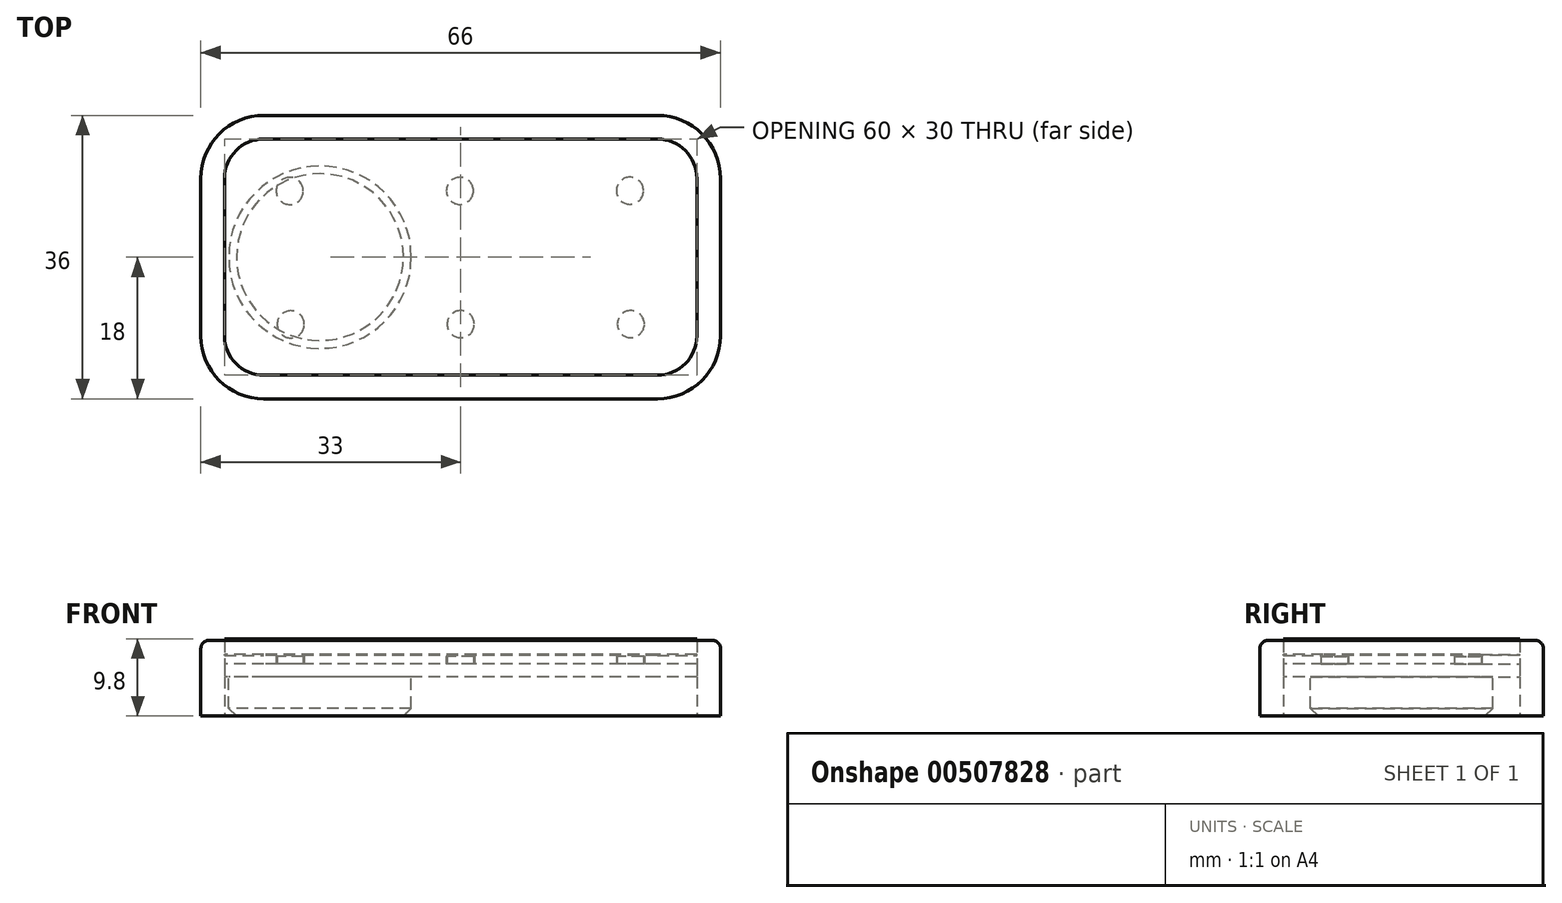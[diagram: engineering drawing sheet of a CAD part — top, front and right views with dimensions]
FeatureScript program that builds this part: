
annotation { "Feature Type Name" : "Feature", "Feature Type Description" : "" }
export const myFeature = defineFeature(function(context is Context, id is Id, definition is map)
    precondition{}
    {
        {
            var Q0;
            Q0=qCreatedBy(makeId("Top.planeOp"),FACE);
            var sketch = newSketch(context, id + "F0", { "sketchPlane" : qUnion([Q0])});
            skLineSegment(sketch, "E0.bottom", {"start": v(25, 15) * mm, "end": v(-25, 15) * mm});
            skLineSegment(sketch, "E0.top", {"start": v(25, -15) * mm, "end": v(-25, -15) * mm});
            skLineSegment(sketch, "E0.left", {"start": v(30, 10) * mm, "end": v(30, -10) * mm});
            skLineSegment(sketch, "E0.right", {"start": v(-30, 10) * mm, "end": v(-30, -10) * mm});
            skPoint(sketch, "E0.middle", {"position": v(0, 0) * mm});
            skPoint(sketch, "E1.visualSharp", {"position": v(-30, 15) * mm});
            skArc(sketch, "E1.filletArc", {"start": v(-25, 15) * mm, "mid": v(-28.54, 13.54) * mm, "end": v(-30, 10) * mm});
            skPoint(sketch, "E2.visualSharp", {"position": v(30, 15) * mm});
            skArc(sketch, "E2.filletArc", {"start": v(30, 10) * mm, "mid": v(28.54, 13.54) * mm, "end": v(25, 15) * mm});
            skPoint(sketch, "E3.visualSharp", {"position": v(30, -15) * mm});
            skArc(sketch, "E3.filletArc", {"start": v(25, -15) * mm, "mid": v(28.54, -13.54) * mm, "end": v(30, -10) * mm});
            skPoint(sketch, "E4.visualSharp", {"position": v(-30, -15) * mm});
            skArc(sketch, "E4.filletArc", {"start": v(-30, -10) * mm, "mid": v(-28.54, -13.54) * mm, "end": v(-25, -15) * mm});
            skArc(sketch, "E5.0", {"start": v(33, 10) * mm, "mid": v(30.66, 15.66) * mm, "end": v(25, 18) * mm});
            skLineSegment(sketch, "E5.1", {"start": v(33, 10) * mm, "end": v(33, -10) * mm});
            skLineSegment(sketch, "E5.2", {"start": v(25, 18) * mm, "end": v(-25, 18) * mm});
            skArc(sketch, "E5.3", {"start": v(25, -18) * mm, "mid": v(30.66, -15.66) * mm, "end": v(33, -10) * mm});
            skArc(sketch, "E5.4", {"start": v(-25, 18) * mm, "mid": v(-30.66, 15.66) * mm, "end": v(-33, 10) * mm});
            skLineSegment(sketch, "E5.5", {"start": v(-33, 10) * mm, "end": v(-33, -10) * mm});
            skArc(sketch, "E5.6", {"start": v(-33, -10) * mm, "mid": v(-30.66, -15.66) * mm, "end": v(-25, -18) * mm});
            skLineSegment(sketch, "E5.7", {"start": v(25, -18) * mm, "end": v(-25, -18) * mm});
            skSolve(sketch);
        }
        {
            var Q0;
            Q0=makeQuery(id+"F0.imprint","IMPRINT",FACE,{"disambiguationData":[TD([[makeQuery(id+"F0.imprint","IMPRINT",EDGE,{"derivedFrom":sQuery(id+"F0.wireOp",EDGE,"E0.bottom")}),1.0]])]});
            var Q1;
            Q1 = qConstructionFilter(qBodyType(qCreatedBy(id + "F0" ,EDGE), BodyType.WIRE), ConstructionObject.NO);
            extrude(context, id + "F1", {"entities" : qUnion([Q0]), "surfaceEntities" : qUnion([Q1]), "depth" : 1.6 * mm});
        }
        {
            var Q0;
            Q0=makeQuery(id+"F1.opExtrude","CAP_FACE",FACE,{"disambiguationData":[OSD([sQuery(id+"F0.wireOp",EDGE,"E0.bottom"),sQuery(id+"F0.wireOp",EDGE,"E0.top"),sQuery(id+"F0.wireOp",EDGE,"E0.left"),sQuery(id+"F0.wireOp",EDGE,"E0.right"),sQuery(id+"F0.wireOp",EDGE,"E1.filletArc"),sQuery(id+"F0.wireOp",EDGE,"E2.filletArc"),sQuery(id+"F0.wireOp",EDGE,"E3.filletArc"),sQuery(id+"F0.wireOp",EDGE,"E4.filletArc")])],"isStart":false});
            extrude(context, id + "F2", {"entities" : qUnion([Q0]), "depth" : 3.2 * mm});
        }
        {
            var Q0;
            Q0=makeQuery(id+"F2.opExtrude","CAP_FACE",FACE,{"disambiguationData":[OSD([sQuery(id+"F0.wireOp",EDGE,"E0.bottom"),sQuery(id+"F0.wireOp",EDGE,"E0.top"),sQuery(id+"F0.wireOp",EDGE,"E0.left"),sQuery(id+"F0.wireOp",EDGE,"E0.right"),sQuery(id+"F0.wireOp",EDGE,"E1.filletArc"),sQuery(id+"F0.wireOp",EDGE,"E2.filletArc"),sQuery(id+"F0.wireOp",EDGE,"E3.filletArc"),sQuery(id+"F0.wireOp",EDGE,"E4.filletArc")])],"isStart":true});
            extrude(context, id + "F3", {"entities" : qUnion([Q0]), "operationType" : NewBodyOperationType.REMOVE, "oppositeDirection" : true, "depth" : 1.2 * mm});
        }
        {
            var Q0;
            Q0=makeQuery(id+"F0.imprint","IMPRINT",FACE,{"disambiguationData":[TD([[makeQuery(id+"F0.imprint","IMPRINT",EDGE,{"derivedFrom":sQuery(id+"F0.wireOp",EDGE,"E0.bottom")}),-1.0]])]});
            extrude(context, id + "F4", {"entities" : qUnion([Q0]), "depth" : 4.6 * mm, "hasSecondDirection" : true, "secondDirectionOppositeDirection" : true, "secondDirectionDepth" : 5 * mm});
        }
        {
            var Q0;
            Q0=makeQuery(id+"F4.opExtrude","CAP_EDGE",EDGE,{"disambiguationData":[OSD([sQuery(id+"F0.wireOp",EDGE,"E5.1")])],"isStart":false});
            fillet(context, id + "F5", {"entities" : qUnion([Q0]), "radius" : 1 * mm, "tangentPropagation" : true, "allowEdgeOverflow" : false});
        }
        {
            var Q0;
            Q0=makeQuery(id+"F0.imprint","IMPRINT",FACE,{"disambiguationData":[TD([[makeQuery(id+"F0.imprint","IMPRINT",EDGE,{"derivedFrom":sQuery(id+"F0.wireOp",EDGE,"E0.bottom")}),1.0]])]});
            var sketch = newSketch(context, id + "F6", { "sketchPlane" : qUnion([Q0])});
            skCircle(sketch, "E6", {"center": v(-17.86, 0) * mm, "radius": 11.59 * mm});
            skSolve(sketch);
        }
        {
            var Q0;
            Q0 = qSketchRegion(id + "F6", true);
            extrude(context, id + "F7", {"entities" : qUnion([Q0]), "oppositeDirection" : true, "depth" : 5 * mm});
        }
        {
            var Q0;
            Q0=makeQuery(id+"F7.opExtrude","CAP_EDGE",EDGE,{"disambiguationData":[OSD([sQuery(id+"F6.wireOp",EDGE,"E6")])],"isStart":false});
            chamfer(context, id + "F8", {"entities" : qUnion([Q0]), "width" : 1 * mm, "tangentPropagation" : true});
        }
        {
            var Q0;
            Q0=makeQuery(id+"F1.opExtrude","CAP_FACE",FACE,{"disambiguationData":[OSD([sQuery(id+"F0.wireOp",EDGE,"E0.bottom"),sQuery(id+"F0.wireOp",EDGE,"E0.top"),sQuery(id+"F0.wireOp",EDGE,"E0.left"),sQuery(id+"F0.wireOp",EDGE,"E0.right"),sQuery(id+"F0.wireOp",EDGE,"E1.filletArc"),sQuery(id+"F0.wireOp",EDGE,"E2.filletArc"),sQuery(id+"F0.wireOp",EDGE,"E3.filletArc"),sQuery(id+"F0.wireOp",EDGE,"E4.filletArc")])],"isStart":false});
            var sketch = newSketch(context, id + "F9", { "sketchPlane" : qUnion([Q0])});
            skCircle(sketch, "E7", {"center": v(-21.7, 8.41) * mm, "radius": 1.72 * mm});
            skCircle(sketch, "E8.1.0.0", {"center": v(-0.1, 8.42) * mm, "radius": 1.72 * mm});
            skCircle(sketch, "E8.2.0.0", {"center": v(21.5, 8.44) * mm, "radius": 1.72 * mm});
            skLineSegment(sketch, "E8.direction1", {"start": v(-21.7, 8.41) * mm, "end": v(-0.1, 8.42) * mm, "construction": true});
            skCircle(sketch, "E9", {"center": v(-21.58, -8.53) * mm, "radius": 1.72 * mm});
            skCircle(sketch, "E10.1.0.0", {"center": v(0.02, -8.52) * mm, "radius": 1.72 * mm});
            skCircle(sketch, "E10.2.0.0", {"center": v(21.62, -8.5) * mm, "radius": 1.72 * mm});
            skLineSegment(sketch, "E10.direction1", {"start": v(-21.58, -8.53) * mm, "end": v(0.02, -8.52) * mm, "construction": true});
            skSolve(sketch);
        }
        {
            var Q0;
            Q0 = qSketchRegion(id + "F9", true);
            extrude(context, id + "F10", {"entities" : qUnion([Q0]), "depth" : 1 * mm});
        }
        {
            var Q0;
            Q0=makeQuery(id+"F3.boolean.opBoolean","COPY",FACE,{"derivedFrom":makeQuery(id+"F3.opExtrude","CAP_FACE",FACE,{"disambiguationData":[OSD([sQuery(id+"F0.wireOp",EDGE,"E0.bottom"),sQuery(id+"F0.wireOp",EDGE,"E0.top"),sQuery(id+"F0.wireOp",EDGE,"E0.left"),sQuery(id+"F0.wireOp",EDGE,"E0.right"),sQuery(id+"F0.wireOp",EDGE,"E1.filletArc"),sQuery(id+"F0.wireOp",EDGE,"E2.filletArc"),sQuery(id+"F0.wireOp",EDGE,"E3.filletArc"),sQuery(id+"F0.wireOp",EDGE,"E4.filletArc")])],"isStart":false})});
            extrude(context, id + "F11", {"entities" : qUnion([Q0]), "depth" : 0.1 * mm});
        }
    });
